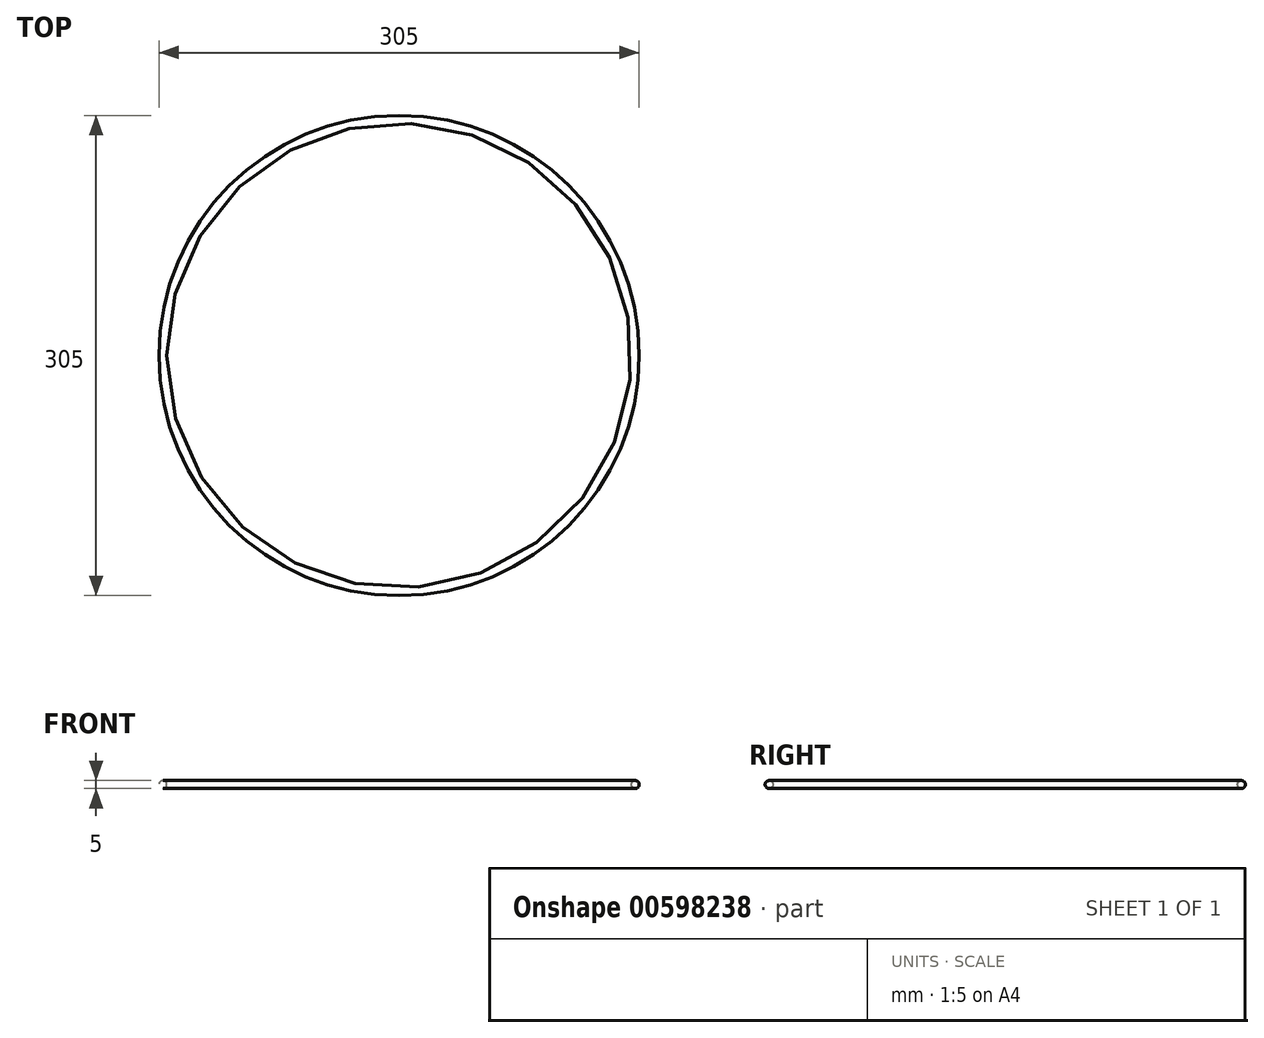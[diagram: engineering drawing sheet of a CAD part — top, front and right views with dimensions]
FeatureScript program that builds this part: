
annotation { "Feature Type Name" : "Feature", "Feature Type Description" : "" }
export const myFeature = defineFeature(function(context is Context, id is Id, definition is map)
    precondition{}
    {
        {
            var Q0;
            Q0=qCreatedBy(makeId("Front.planeOp"),FACE);
            var sketch = newSketch(context, id + "F0", { "sketchPlane" : qUnion([Q0])});
            skCircle(sketch, "E0", {"center": v(-150, 0) * mm, "radius": 2.5 * mm});
            skLineSegment(sketch, "E1", {"start": v(0, 0) * mm, "end": v(0, 7.65) * mm, "construction": true});
            skCircle(sketch, "E2", {"center": v(-109.63, -33.9) * mm, "radius": 2.5 * mm});
            skCircle(sketch, "E3", {"center": v(-61.86, -80.19) * mm, "radius": 2.5 * mm});
            skSolve(sketch);
        }
        {
            var Q0;
            Q0=makeQuery(id+"F0.imprint","IMPRINT",FACE,{"disambiguationData":[TD([[makeQuery(id+"F0.imprint","IMPRINT",EDGE,{"derivedFrom":sQuery(id+"F0.wireOp",EDGE,"E0")}),1.0]])]});
            var Q1;
            Q1=sQuery(id+"F0.wireOp",EDGE,"E1");
            revolve(context, id + "F1", {"entities" : qUnion([Q0]), "axis" : qUnion([Q1]), "revolveType" : RevolveType.FULL});
        }
    });
